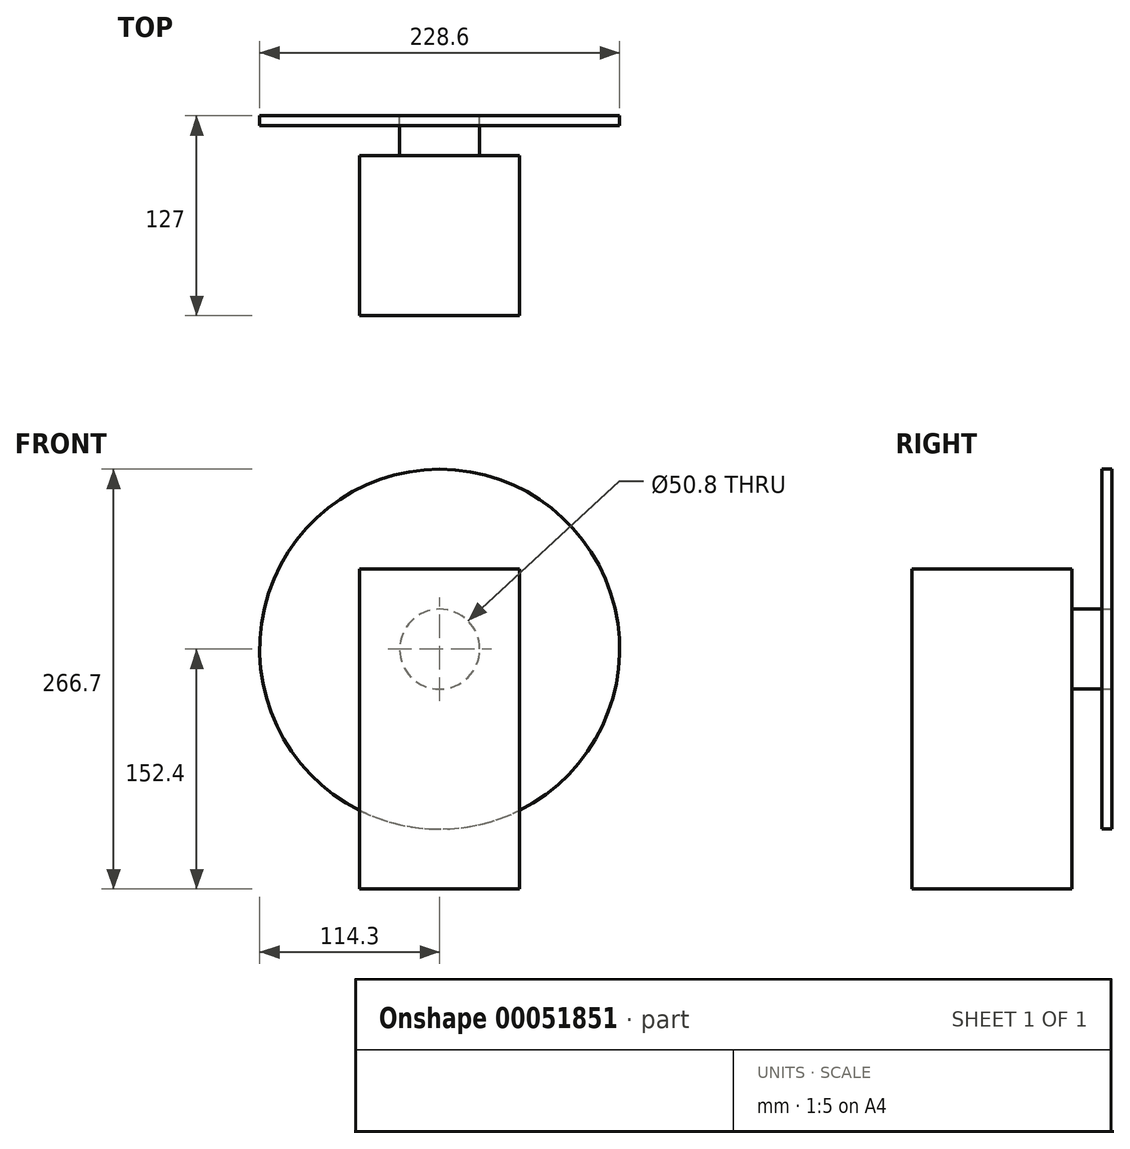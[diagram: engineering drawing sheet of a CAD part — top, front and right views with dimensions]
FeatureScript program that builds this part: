
annotation { "Feature Type Name" : "Feature", "Feature Type Description" : "" }
export const myFeature = defineFeature(function(context is Context, id is Id, definition is map)
    precondition{}
    {
        {
            var Q0;
            Q0=qCreatedBy(makeId("Right.planeOp"),FACE);
            var sketch = newSketch(context, id + "F0", { "sketchPlane" : qUnion([Q0])});
            skLineSegment(sketch, "E0.bottom", {"start": v(-101.6, 83.66) * mm, "end": v(0, 83.66) * mm});
            skLineSegment(sketch, "E0.top", {"start": v(-101.6, -119.54) * mm, "end": v(0, -119.54) * mm});
            skLineSegment(sketch, "E0.left", {"start": v(-101.6, 83.66) * mm, "end": v(-101.6, -119.54) * mm});
            skLineSegment(sketch, "E0.right", {"start": v(0, 83.66) * mm, "end": v(0, -119.54) * mm});
            skSolve(sketch);
        }
        {
            var Q0;
            Q0=makeQuery(id+"F0.imprint","IMPRINT",FACE,{"disambiguationData":[TD([[makeQuery(id+"F0.imprint","IMPRINT",EDGE,{"derivedFrom":sQuery(id+"F0.wireOp",EDGE,"E0.bottom")}),-1.0]])]});
            extrude(context, id + "F1", {"entities" : qUnion([Q0]), "depth" : 101.6 * mm});
        }
        {
            var Q0;
            Q0=makeQuery(id+"F1.opExtrude","SWEPT_FACE",FACE,{"disambiguationData":[OSD([sQuery(id+"F0.wireOp",EDGE,"E0.right")])]});
            var sketch = newSketch(context, id + "F2", { "sketchPlane" : qUnion([Q0])});
            skCircle(sketch, "E1", {"center": v(-50.8, 32.86) * mm, "radius": 25.4 * mm});
            skSolve(sketch);
        }
        {
            var Q0;
            Q0=makeQuery(id+"F2.imprint","IMPRINT",FACE,{"disambiguationData":[TD([[makeQuery(id+"F2.imprint","IMPRINT",EDGE,{"derivedFrom":sQuery(id+"F2.wireOp",EDGE,"E1")}),1.0]])]});
            extrude(context, id + "F3", {"entities" : qUnion([Q0]), "operationType" : NewBodyOperationType.ADD, "depth" : 25.4 * mm});
        }
        {
            var Q0;
            Q0=makeQuery(id+"F3.opExtrude","CAP_FACE",FACE,{"disambiguationData":[OSD([sQuery(id+"F2.wireOp",EDGE,"E1")])],"isStart":false});
            var sketch = newSketch(context, id + "F4", { "sketchPlane" : qUnion([Q0])});
            skCircle(sketch, "E2", {"center": v(-50.8, 32.86) * mm, "radius": 114.3 * mm});
            skSolve(sketch);
        }
        {
            var Q0;
            Q0=makeQuery(id+"F4.imprint","IMPRINT",FACE,{"disambiguationData":[TD([[makeQuery(id+"F4.imprint","IMPRINT",EDGE,{"derivedFrom":sQuery(id+"F4.wireOp",EDGE,"E2")}),1.0]])]});
            extrude(context, id + "F5", {"entities" : qUnion([Q0]), "oppositeDirection" : true, "depth" : 6.35 * mm});
        }
    });
